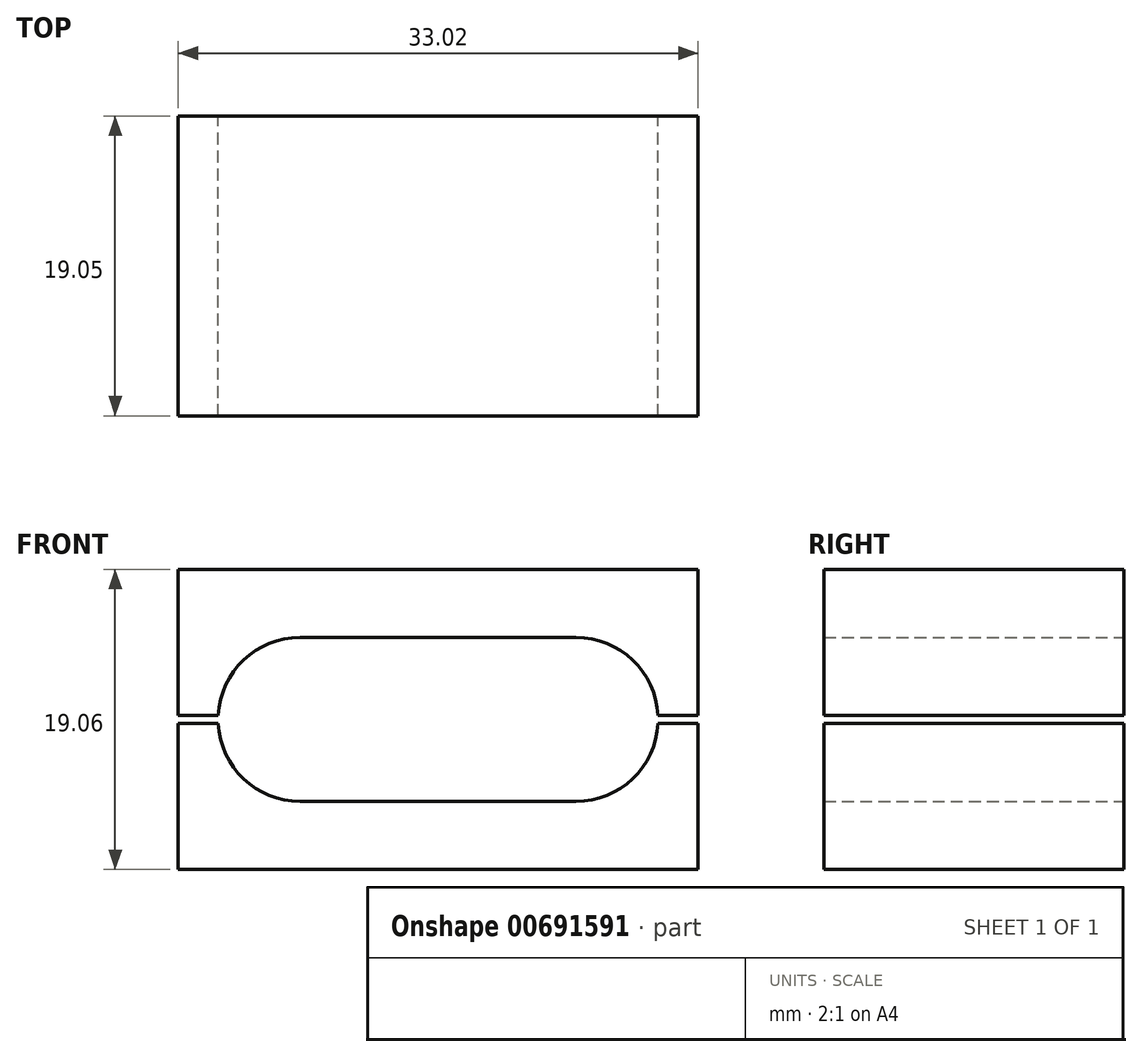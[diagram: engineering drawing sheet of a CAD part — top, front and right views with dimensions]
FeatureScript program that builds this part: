
annotation { "Feature Type Name" : "Feature", "Feature Type Description" : "" }
export const myFeature = defineFeature(function(context is Context, id is Id, definition is map)
    precondition{}
    {
        {
            var Q0;
            Q0=qCreatedBy(makeId("Front.planeOp"),FACE);
            var sketch = newSketch(context, id + "F0", { "sketchPlane" : qUnion([Q0])});
            skCircle(sketch, "E0", {"center": v(-17.53, 0) * mm, "radius": 5.2 * mm});
            skCircle(sketch, "E1", {"center": v(0, 0) * mm, "radius": 5.2 * mm});
            skLineSegment(sketch, "E2", {"start": v(-17.53, 5.2) * mm, "end": v(0, 5.2) * mm});
            skLineSegment(sketch, "E3", {"start": v(-17.53, -5.2) * mm, "end": v(0, -5.2) * mm});
            skLineSegment(sketch, "E4", {"start": v(-22.73, 0) * mm, "end": v(5.2, 0) * mm, "construction": true});
            skPoint(sketch, "E5", {"position": v(-8.76, 0) * mm});
            skLineSegment(sketch, "E6.bottom", {"start": v(7.75, -9.53) * mm, "end": v(-18.29, -9.52) * mm});
            skLineSegment(sketch, "E6.top", {"start": v(7.75, 9.53) * mm, "end": v(-25.27, 9.53) * mm});
            skLineSegment(sketch, "E6.left", {"start": v(7.75, -9.53) * mm, "end": v(7.75, 9.52) * mm});
            skLineSegment(sketch, "E6.right", {"start": v(-25.27, -9.52) * mm, "end": v(-25.27, 9.53) * mm});
            skLineSegment(sketch, "E7.bottom", {"start": v(7.75, -0.25) * mm, "end": v(-25.27, -0.25) * mm});
            skLineSegment(sketch, "E7.top", {"start": v(7.75, 0.25) * mm, "end": v(-25.27, 0.25) * mm});
            skLineSegment(sketch, "E7.left", {"start": v(7.75, -0.25) * mm, "end": v(7.75, 0.25) * mm});
            skLineSegment(sketch, "E7.right", {"start": v(-25.27, -0.25) * mm, "end": v(-25.27, 0.25) * mm});
            skLineSegment(sketch, "E8.bottom", {"start": v(-18.29, -9.52) * mm, "end": v(0.76, -9.52) * mm});
            skLineSegment(sketch, "E8.top", {"start": v(-18.29, -15.88) * mm, "end": v(0.76, -15.88) * mm});
            skLineSegment(sketch, "E8.left", {"start": v(-18.29, -9.52) * mm, "end": v(-18.29, -15.88) * mm});
            skLineSegment(sketch, "E8.right", {"start": v(0.76, -9.53) * mm, "end": v(0.76, -15.88) * mm});
            skLineSegment(sketch, "E9", {"start": v(-18.29, -9.52) * mm, "end": v(-25.27, -9.52) * mm});
            skSolve(sketch);
        }
        {
            var Q0;
            Q0=makeQuery(id+"F0.imprint","IMPRINT",FACE,{"disambiguationData":[TD([[makeQuery(id+"F0.imprint","IMPRINT",EDGE,{"derivedFrom":sQuery(id+"F0.wireOp",EDGE,"E8.bottom")}),-1.0]])]});
            var Q1;
            {var subQ1=sQuery(id+"F0.wireOp",EDGE,"E3");Q1=makeQuery(id+"F0.imprint","IMPRINT",FACE,{"disambiguationData":[TD([[makeQuery(id+"F0.imprint","IMPRINT",EDGE,{"derivedFrom":subQ1}),-1.0]])]});}
            var Q2;
            {var subQ1=sQuery(id+"F0.wireOp",EDGE,"E2");Q2=makeQuery(id+"F0.imprint","IMPRINT",FACE,{"disambiguationData":[TD([[makeQuery(id+"F0.imprint","IMPRINT",EDGE,{"derivedFrom":subQ1}),1.0]])]});}
            extrude(context, id + "F1", {"entities" : qUnion([Q0, Q1, Q2]), "depth" : 19.05 * mm, "offsetDistance" : 25.4 * mm});
        }
    });
